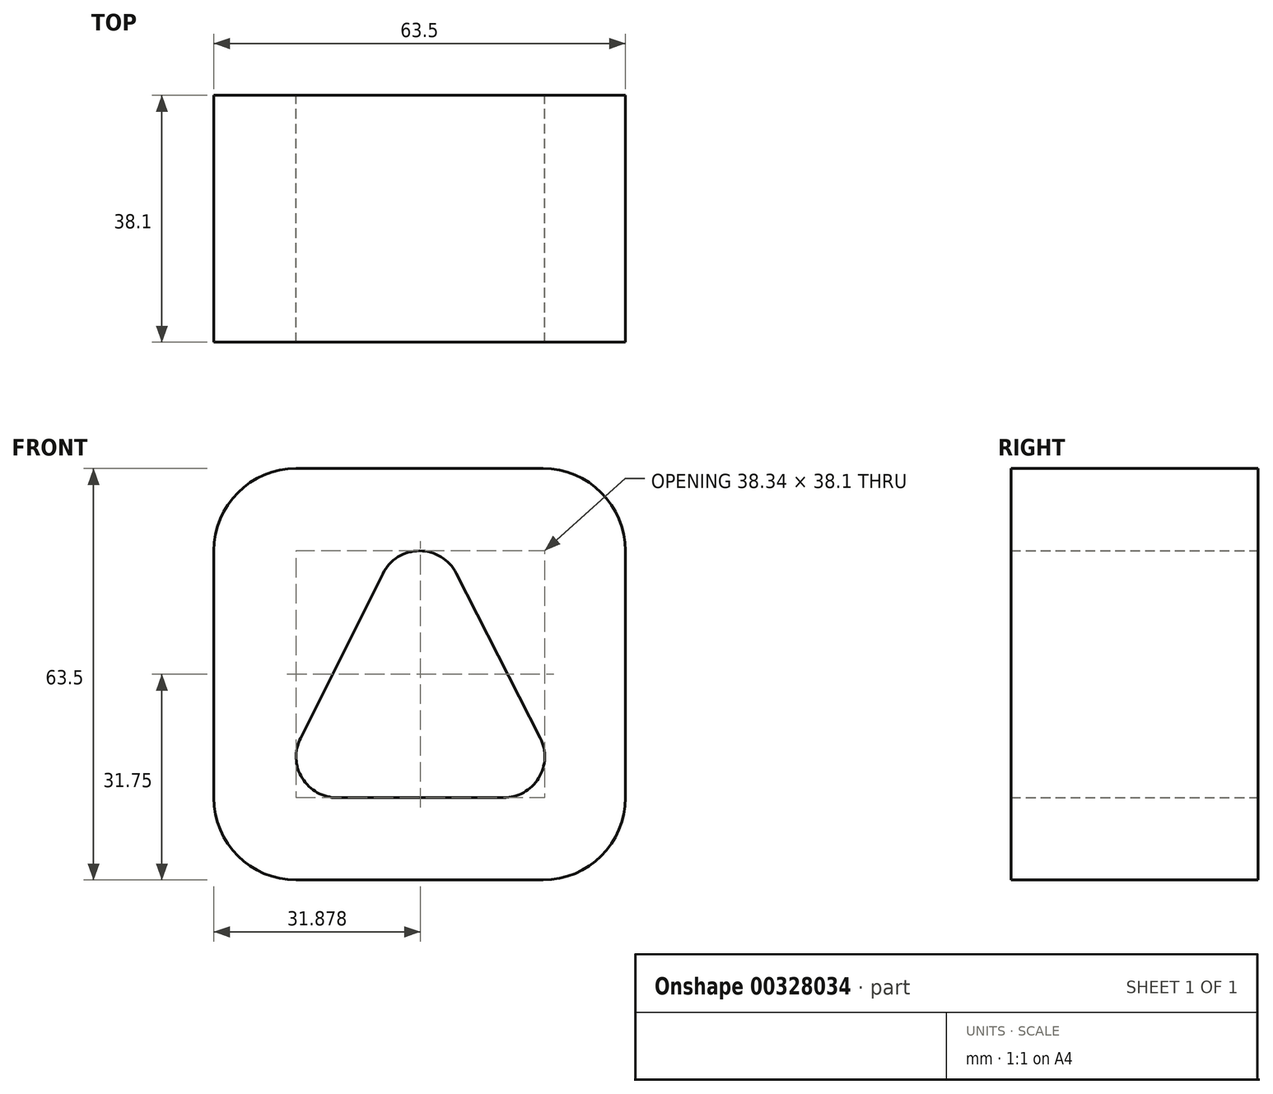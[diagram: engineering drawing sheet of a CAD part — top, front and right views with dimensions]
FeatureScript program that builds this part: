
annotation { "Feature Type Name" : "Feature", "Feature Type Description" : "" }
export const myFeature = defineFeature(function(context is Context, id is Id, definition is map)
    precondition{}
    {
        {
            var Q0;
            Q0=qCreatedBy(makeId("Front.planeOp"),FACE);
            var sketch = newSketch(context, id + "F0", { "sketchPlane" : qUnion([Q0])});
            skLineSegment(sketch, "E0", {"start": v(0, 0) * mm, "end": v(63.5, 0) * mm});
            skLineSegment(sketch, "E1", {"start": v(63.5, 0) * mm, "end": v(63.5, 63.5) * mm});
            skLineSegment(sketch, "E2", {"start": v(63.5, 63.5) * mm, "end": v(0, 63.5) * mm});
            skArc(sketch, "E3", {"start": v(37.4, 47.33) * mm, "mid": v(31.72, 50.8) * mm, "end": v(26.07, 47.29) * mm});
            skArc(sketch, "E4", {"start": v(44.7, 12.7) * mm, "mid": v(50.12, 15.73) * mm, "end": v(50.36, 21.93) * mm});
            skArc(sketch, "E5", {"start": v(13.37, 21.89) * mm, "mid": v(13.65, 15.71) * mm, "end": v(19.05, 12.7) * mm});
            skLineSegment(sketch, "E6", {"start": v(37.4, 47.33) * mm, "end": v(50.36, 21.93) * mm});
            skLineSegment(sketch, "E7", {"start": v(44.7, 12.7) * mm, "end": v(19.05, 12.7) * mm});
            skLineSegment(sketch, "E8", {"start": v(13.37, 21.89) * mm, "end": v(26.07, 47.29) * mm});
            skLineSegment(sketch, "E9", {"start": v(0, 0) * mm, "end": v(0, 63.5) * mm});
            skSolve(sketch);
        }
        {
            var Q0;
            Q0=makeQuery(id+"F0.imprint","IMPRINT",FACE,{"disambiguationData":[TD([[makeQuery(id+"F0.imprint","IMPRINT",EDGE,{"derivedFrom":sQuery(id+"F0.wireOp",EDGE,"E0")}),1.0]])]});
            extrude(context, id + "F1", {"entities" : qUnion([Q0]), "depth" : 38.1 * mm});
        }
        {
            var Q0;
            Q0=makeQuery(id+"F1.opExtrude","SWEPT_EDGE",EDGE,{"disambiguationData":[OSD([sQuery(id+"F0.wireOp",EDGE,"E0"),sQuery(id+"F0.wireOp",EDGE,"E1")])]});
            var Q1;
            Q1=makeQuery(id+"F1.opExtrude","SWEPT_EDGE",EDGE,{"disambiguationData":[OSD([sQuery(id+"F0.wireOp",EDGE,"E1"),sQuery(id+"F0.wireOp",EDGE,"E2")])]});
            var Q2;
            Q2=makeQuery(id+"F1.opExtrude","SWEPT_EDGE",EDGE,{"disambiguationData":[OSD([sQuery(id+"F0.wireOp",EDGE,"E2"),sQuery(id+"F0.wireOp",EDGE,"E9")])]});
            var Q3;
            Q3=makeQuery(id+"F1.opExtrude","SWEPT_EDGE",EDGE,{"disambiguationData":[OSD([sQuery(id+"F0.wireOp",EDGE,"E0"),sQuery(id+"F0.wireOp",EDGE,"E9")])]});
            fillet(context, id + "F2", {"entities" : qUnion([Q0, Q1, Q2, Q3]), "radius" : 12.7 * mm, "tangentPropagation" : true, "allowEdgeOverflow" : false});
        }
    });
